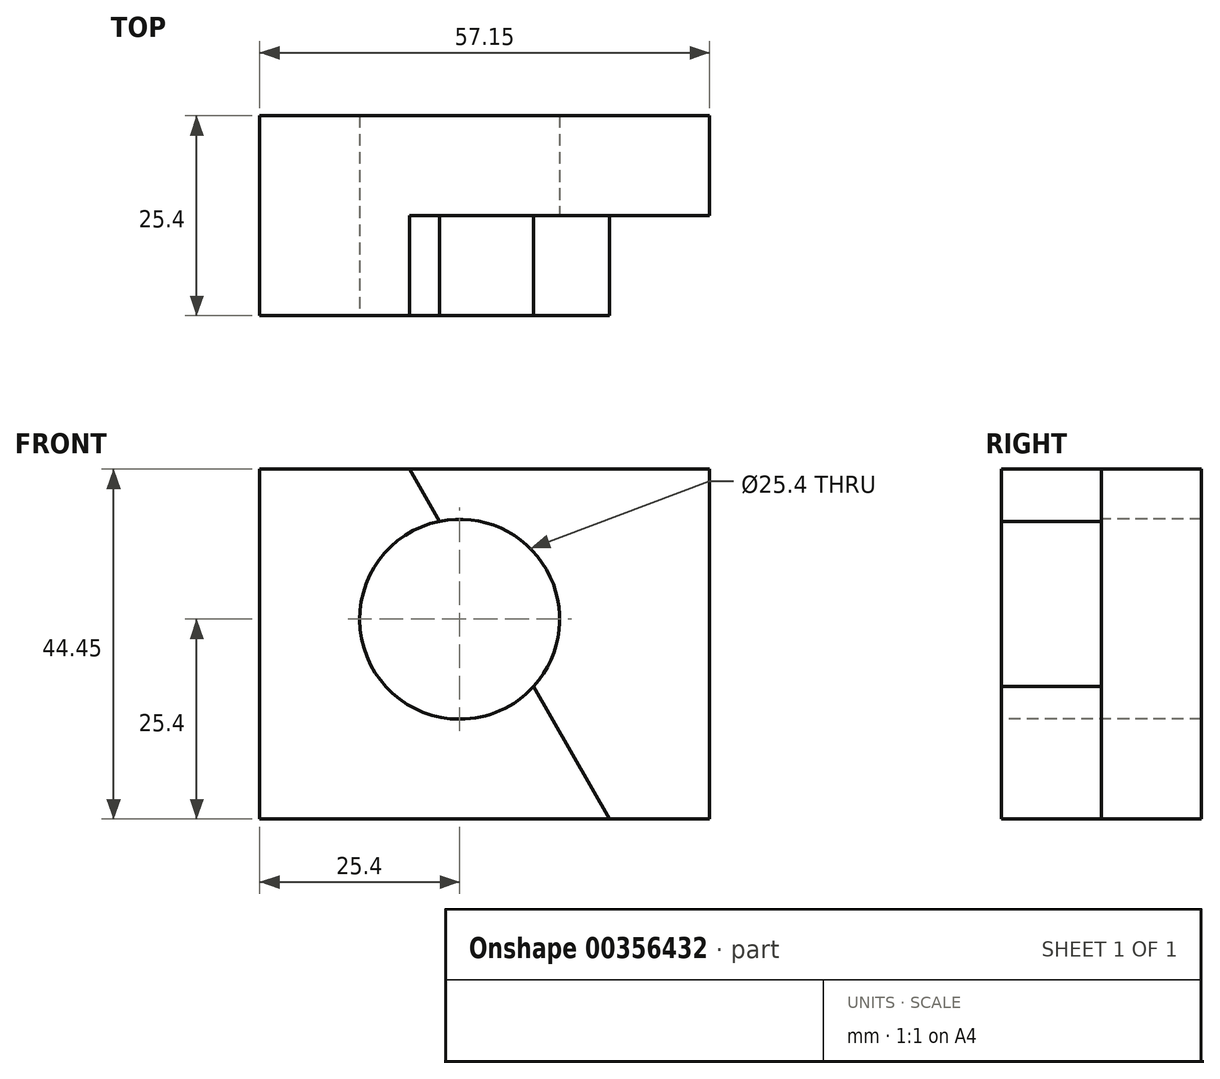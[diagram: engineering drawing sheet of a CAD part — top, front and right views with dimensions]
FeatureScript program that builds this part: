
annotation { "Feature Type Name" : "Feature", "Feature Type Description" : "" }
export const myFeature = defineFeature(function(context is Context, id is Id, definition is map)
    precondition{}
    {
        {
            var Q0;
            Q0=qCreatedBy(makeId("Front.planeOp"),FACE);
            var sketch = newSketch(context, id + "F0", { "sketchPlane" : qUnion([Q0])});
            skLineSegment(sketch, "E0.bottom", {"start": v(0, 0) * mm, "end": v(57.15, 0) * mm});
            skLineSegment(sketch, "E0.top", {"start": v(0, 44.45) * mm, "end": v(57.15, 44.45) * mm});
            skLineSegment(sketch, "E0.left", {"start": v(0, 0) * mm, "end": v(0, 44.45) * mm});
            skLineSegment(sketch, "E0.right", {"start": v(57.15, 0) * mm, "end": v(57.15, 44.45) * mm});
            skSolve(sketch);
        }
        {
            var Q0;
            Q0=makeQuery(id+"F0.imprint","IMPRINT",FACE,{"disambiguationData":[TD([[makeQuery(id+"F0.imprint","IMPRINT",EDGE,{"derivedFrom":sQuery(id+"F0.wireOp",EDGE,"E0.bottom")}),1.0]])]});
            extrude(context, id + "F1", {"entities" : qUnion([Q0]), "depth" : 25.4 * mm});
        }
        {
            var Q0;
            Q0=makeQuery(id+"F1.opExtrude","CAP_FACE",FACE,{"disambiguationData":[OSD([sQuery(id+"F0.wireOp",EDGE,"E0.bottom"),sQuery(id+"F0.wireOp",EDGE,"E0.top"),sQuery(id+"F0.wireOp",EDGE,"E0.left"),sQuery(id+"F0.wireOp",EDGE,"E0.right")])],"isStart":false});
            var sketch = newSketch(context, id + "F2", { "sketchPlane" : qUnion([Q0])});
            skCircle(sketch, "E1", {"center": v(25.4, 25.4) * mm, "radius": 12.7 * mm});
            skSolve(sketch);
        }
        {
            var Q0;
            Q0=makeQuery(id+"F2.imprint","IMPRINT",FACE,{"disambiguationData":[TD([[makeQuery(id+"F2.imprint","IMPRINT",EDGE,{"derivedFrom":sQuery(id+"F2.wireOp",EDGE,"E1")}),1.0]])]});
            extrude(context, id + "F3", {"entities" : qUnion([Q0]), "operationType" : NewBodyOperationType.REMOVE, "oppositeDirection" : true, "depth" : 25.4 * mm});
        }
        {
            var Q0;
            Q0=makeQuery(id+"F1.opExtrude","CAP_FACE",FACE,{"disambiguationData":[OSD([sQuery(id+"F0.wireOp",EDGE,"E0.bottom"),sQuery(id+"F0.wireOp",EDGE,"E0.top"),sQuery(id+"F0.wireOp",EDGE,"E0.left"),sQuery(id+"F0.wireOp",EDGE,"E0.right")])],"isStart":false});
            var sketch = newSketch(context, id + "F4", { "sketchPlane" : qUnion([Q0])});
            skLineSegment(sketch, "E2", {"start": v(19.05, 44.45) * mm, "end": v(44.45, 0) * mm});
            skSolve(sketch);
        }
        {
            var Q0;
            Q0 = qSketchRegion(id + "F4", true);
            var Q1;
            {var subQ0=makeQuery(id+"F1.opExtrude","CAP_EDGE",EDGE,{"disambiguationData":[OSD([sQuery(id+"F0.wireOp",EDGE,"E0.right")])],"isStart":false});Q1=makeQuery(id+"F4.imprint","IMPRINT",FACE,{"disambiguationData":[TD([[makeQuery(id+"F4.imprint","IMPRINT",EDGE,{"derivedFrom":subQ0}),1.0]])]});}
            extrude(context, id + "F5", {"entities" : qUnion([Q0, Q1]), "operationType" : NewBodyOperationType.REMOVE, "oppositeDirection" : true, "depth" : 12.7 * mm});
        }
    });
